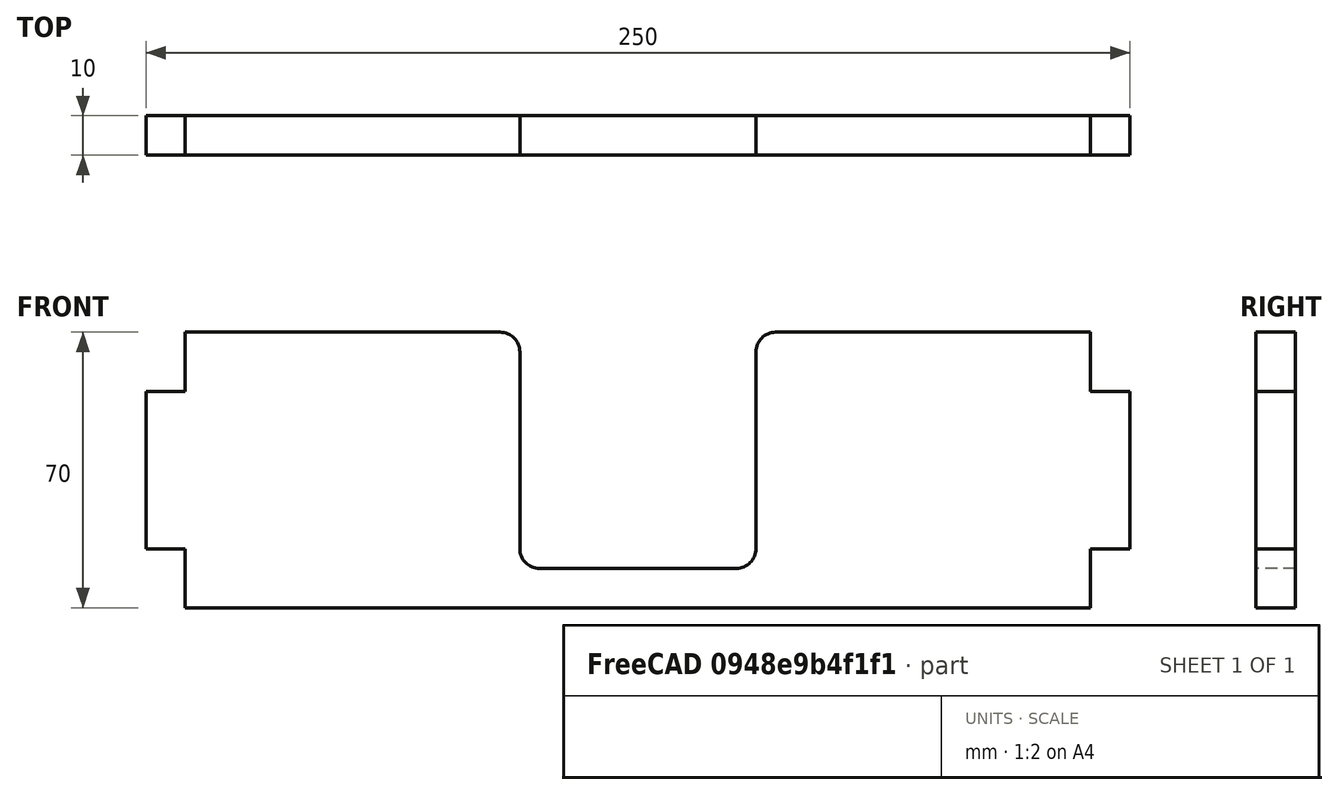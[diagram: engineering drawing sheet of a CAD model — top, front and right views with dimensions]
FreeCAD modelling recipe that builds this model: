
FCSTD DOCUMENT  (FreeCAD 0.19R19327 (Git))
Label: Soporte_Motor
License: All rights reserved
LicenseURL: http://en.wikipedia.org/wiki/All_rights_reserved
objects: Sketcher::SketchObject×1, PartDesign::Pad×1, PartDesign::Body×1
note: 4 computed .brp shape members not serialized (recipe doc carries the construction recipe); baked Part::Feature solids carry a one-line shape summary decoded from their .brp

FEATURE [Sketcher::SketchObject] Sketch
  MapMode = 5
  Placement = pos=(0,0,0) rot=(1,0,0;1.5708rad)
  Support = -> [XZ_Plane]
  sketch-geometry (20):
    g0: LineSegment StartX=0 StartY=0 StartZ=0 EndX=0 EndY=15 EndZ=0
    g1: LineSegment StartX=0 StartY=15 StartZ=0 EndX=-10 EndY=15 EndZ=0
    g2: LineSegment StartX=-10 StartY=15 StartZ=0 EndX=-10 EndY=55 EndZ=0
    g3: LineSegment StartX=-10 StartY=55 StartZ=0 EndX=0 EndY=55 EndZ=0
    g4: LineSegment StartX=0 StartY=55 StartZ=0 EndX=0 EndY=70 EndZ=0
    g5: LineSegment StartX=0 StartY=70 StartZ=0 EndX=80 EndY=70 EndZ=0
    g6: LineSegment StartX=85 StartY=65 StartZ=0 EndX=85 EndY=15 EndZ=0
    g7: LineSegment StartX=90 StartY=10 StartZ=0 EndX=140 EndY=10 EndZ=0
    g8: LineSegment StartX=145 StartY=15 StartZ=0 EndX=145 EndY=65 EndZ=0
    g9: LineSegment StartX=150 StartY=70 StartZ=0 EndX=230 EndY=70 EndZ=0
    g10: LineSegment StartX=230 StartY=70 StartZ=0 EndX=230 EndY=55 EndZ=0
    g11: LineSegment StartX=230 StartY=55 StartZ=0 EndX=240 EndY=55 EndZ=0
    g12: LineSegment StartX=240 StartY=55 StartZ=0 EndX=240 EndY=15 EndZ=0
    g13: LineSegment StartX=240 StartY=15 StartZ=0 EndX=230 EndY=15 EndZ=0
    g14: LineSegment StartX=230 StartY=15 StartZ=0 EndX=230 EndY=-8.5194e-12 EndZ=0
    g15: LineSegment StartX=230 StartY=-8.5194e-12 StartZ=0 EndX=0 EndY=0 EndZ=0
    g16: ArcOfCircle CenterX=90 CenterY=15 CenterZ=0 NormalX=0 NormalY=0 NormalZ=1 AngleXU=0 Radius=5 StartAngle=3.14159 EndAngle=4.71239
    g17: ArcOfCircle CenterX=140 CenterY=15 CenterZ=0 NormalX=0 NormalY=0 NormalZ=1 AngleXU=0 Radius=5 StartAngle=4.71239 EndAngle=6.28319
    g18: ArcOfCircle CenterX=150 CenterY=65 CenterZ=0 NormalX=0 NormalY=0 NormalZ=1 AngleXU=0 Radius=5 StartAngle=1.5708 EndAngle=3.14159
    g19: ArcOfCircle CenterX=80 CenterY=65 CenterZ=0 NormalX=0 NormalY=0 NormalZ=1 AngleXU=0 Radius=5 StartAngle=-9e-16 EndAngle=1.5708
  constraints (55):
    c: Coincident(g-1,g0)
    c: PointOnObject(g0,g-2)
    c: Coincident(g0,g1)
    c: Horizontal(g1)
    c: Coincident(g1,g2)
    c: Vertical(g2)
    c: Coincident(g2,g3)
    c: Horizontal(g3)
    c: Coincident(g3,g4)
    c: PointOnObject(g4,g-2)
    c: Coincident(g4,g5)
    c: Horizontal(g5)
    c: Vertical(g6)
    c: Horizontal(g7)
    c: Vertical(g8)
    c: Horizontal(g9)
    c: Coincident(g9,g10)
    c: Vertical(g10)
    c: Coincident(g10,g11)
    c: Horizontal(g11)
    c: Coincident(g11,g12)
    c: Vertical(g12)
    c: Coincident(g12,g13)
    c: Horizontal(g13)
    c: Coincident(g13,g14)
    c: Vertical(g14)
    c: Coincident(g14,g15)
    c: Coincident(g15,g0)
    c: Equal(g2,g12)
    c: Equal(g4,g10)
    c: Equal(g10,g14)
    c: Equal(g14,g0)
    c: Equal(g8,g6)
    c: Tangent(g6,g16) = -1.5708
    c: Tangent(g7,g16) = -1.5708
    c: Tangent(g7,g17) = -1.5708
    c: Tangent(g8,g17) = -1.5708
    c: Tangent(g8,g18) = 1.5708
    c: Tangent(g9,g18) = 1.5708
    c: Tangent(g6,g19) = 1.5708
    c: Tangent(g5,g19) = 1.5708
    c: Equal(g19,g16)
    c: Equal(g16,g17)
    c: Equal(g17,g18)
    c: Radius(g19) = 5
    c: DistanceY(g2,g2) = 40
    c: DistanceY(g0,g0) = 15
    c: Equal(g1,g3)
    c: Equal(g3,g11)
    c: Equal(g11,g13)
    c: DistanceX(g11,g11) = 10
    c: DistanceX(g15,g15) = 230
    c: Equal(g9,g5)
    c: DistanceX(g9,g9) = 80
    c: DistanceY(g8,g8) = 50
FEATURE [PartDesign::Pad] Pad
  Length = 10
  Length2 = 100
  Placement = pos=(0,0,0) rot=(1,0,0;1.5708rad)
  Profile = -> Sketch
  Type = 0
FEATURE [PartDesign::Body] Body
  Group = -> [Sketch,Pad]
  Origin = -> Origin
  Tip = -> Pad
